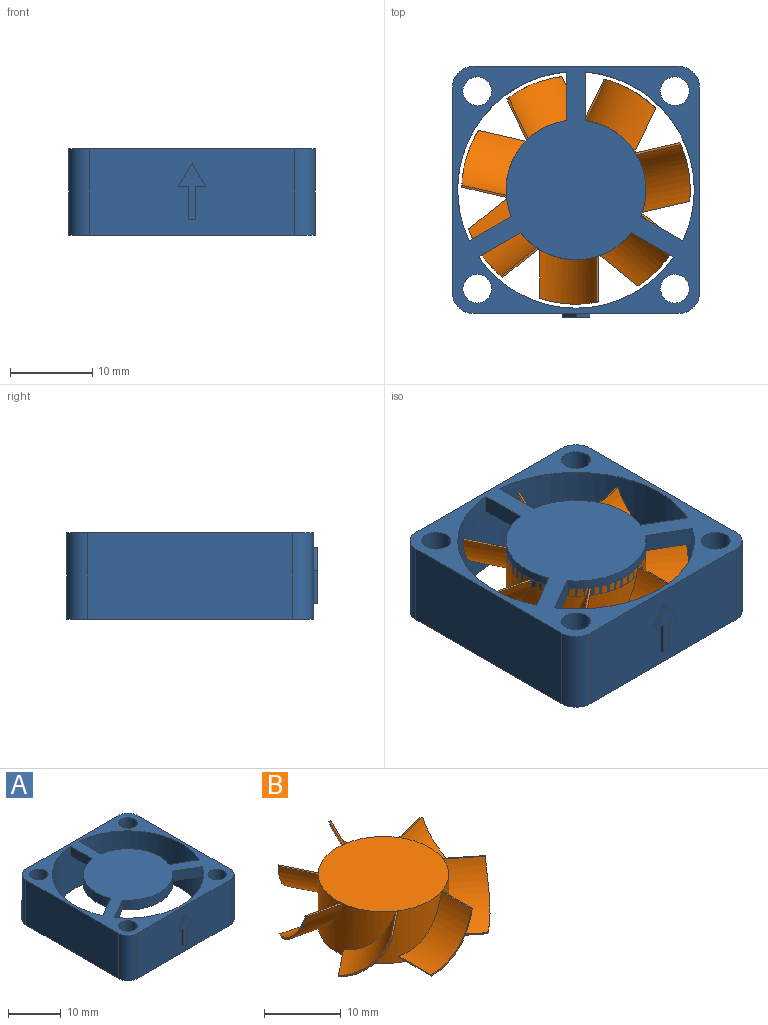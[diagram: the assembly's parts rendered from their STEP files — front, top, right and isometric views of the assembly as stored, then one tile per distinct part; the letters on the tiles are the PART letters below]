
ASSEMBLY  parts=2 mates=1
PART A: 33 faces, bbox 30x30.5x10.5 mm
  f0: cylinder r=2.5mm len=10.5mm, axis (0,0,-1), area 41.2mm2, adj f16,f25,f26,f28
  f1: cylinder r=2.5mm len=10.5mm, axis (0,0,1), area 41.2mm2, adj f4,f16,f25,f26
  f2: cylinder r=2.5mm len=10.5mm, axis (0,0,1), area 41.2mm2, adj f16,f26,f28,f29
  f3: cylinder r=14.38mm len=28.75mm, axis (0,0,1), area 932.8mm2, adj f7,f10,f11,f12,f13,f14,f15,f16
  f4: plane 25x10.5mm, normal (1,0,0), area 262.5mm2, adj f1,f5,f16,f26
  f5: cylinder r=2.5mm len=10.5mm, axis (0,0,-1), area 41.2mm2, adj f4,f16,f26,f29
  f6: cylinder r=8.5mm len=11.64mm, axis (0,0,-1), area 34.9mm2, adj f7,f14,f15,f26
  f7: plane 5.12x2.95mm, normal (0.5,0.87,0), area 13.3mm2, adj f3,f6,f15,f26
  f8: cylinder r=8.5mm len=11.64mm, axis (0,0,-1), area 34.9mm2, adj f12,f13,f15,f26
  f9: cylinder r=8.5mm len=13.44mm, axis (0,0,-1), area 34.9mm2, adj f10,f11,f15,f26
  f10: plane 5.12x2.95mm, normal (-0.5,-0.87,0), area 13.3mm2, adj f3,f9,f15,f26
  f11: plane 5.12x2.95mm, normal (0.5,-0.87,0), area 13.3mm2, adj f3,f9,f15,f26
  f12: plane 5.12x2.95mm, normal (-0.5,0.87,0), area 13.3mm2, adj f3,f8,f15,f26
  f13: plane 5.91x2.25mm, normal (-1,0,0), area 13.3mm2, adj f3,f8,f15,f26
  f14: plane 5.91x2.25mm, normal (1,0,0), area 13.3mm2, adj f3,f6,f15,f26
  f15: plane 25.97x22.88mm, normal (0,0,-1), area 267.6mm2, adj f3,f6,f7,f8,f9,f10,f11,f12
  f16: plane 30x30mm, normal (0,0,-1), area 207mm2, adj f0,f1,f2,f3,f4,f5,f25,f27
  f17: plane 0.95x0.5mm, normal (0,0,-1), area 0.5mm2, adj f18,f19,f24,f25
  f18: plane 4.03x0.5mm, normal (1,0,0), area 2mm2, adj f17,f20,f24,f25
  f19: plane 4.03x0.5mm, normal (-1,0,0), area 2mm2, adj f17,f23,f24,f25
  f20: plane 1.22x0.5mm, normal (0,0,-1), area 0.6mm2, adj f18,f21,f24,f25
  f21: plane 2.81x1.7mm, normal (0.86,0,0.52), area 1.6mm2, adj f20,f22,f24,f25
  f22: plane 2.81x1.7mm, normal (-0.86,0,0.52), area 1.6mm2, adj f21,f23,f24,f25
  f23: plane 1.22x0.5mm, normal (0,0,-1), area 0.6mm2, adj f19,f22,f24,f25
  f24: plane 6.84x3.39mm, normal (0,-1,0), area 8.6mm2, adj f17,f18,f19,f20,f21,f22,f23
  f25: plane 25x10.5mm, normal (0,-1,0), area 253.9mm2, adj f0,f1,f16,f17,f18,f19,f20,f21
  f26: plane 30x30mm, normal (0,0,1), area 474.6mm2, adj f0,f1,f2,f3,f4,f5,f6,f7
  f27: cylinder r=1.75mm len=10.5mm, axis (0,0,1), area 115.5mm2, adj f16,f26
  f28: plane 25x10.5mm, normal (-1,0,0), area 262.5mm2, adj f0,f2,f16,f26
  f29: plane 25x10.5mm, normal (0,1,0), area 262.5mm2, adj f2,f5,f16,f26
  f30: cylinder r=1.75mm len=10.5mm, axis (0,0,1), area 115.5mm2, adj f16,f26
  f31: cylinder r=1.75mm len=10.5mm, axis (0,0,1), area 115.5mm2, adj f16,f26
  f32: cylinder r=1.75mm len=10.5mm, axis (0,0,1), area 115.5mm2, adj f16,f26
PART B: 39 faces, bbox 28.2x28.1x8.3 mm
  f0: cylinder r=10.55mm len=9.5mm, axis (0.78,0.62,0), area 61.5mm2, adj f1,f19,f25,f37
  f1: cylinder r=13.88mm len=7.49mm, axis (0,0,1), area 2.7mm2, adj f0,f19,f20,f25
  f2: cylinder r=10.3mm len=7.25mm, axis (0,1,0), area 60mm2, adj f10,f11,f26,f37
  f3: cylinder r=10.3mm len=9.42mm, axis (-0.78,0.62,0), area 60mm2, adj f7,f22,f27,f37
  f4: plane 5.75x1.39mm, normal (0.21,-0.93,-0.29), area 1.5mm2, adj f5,f8,f28,f37
  f5: cylinder r=10.3mm len=8.21mm, axis (-0.97,-0.22,0), area 55.8mm2, adj f4,f28,f33,f37,f38
  f6: cylinder r=10.55mm len=9.5mm, axis (-0.78,0.62,0), area 61.5mm2, adj f7,f22,f27,f37
  f7: plane 4.44x3.69mm, normal (0.16,0.2,0.97), area 1.4mm2, adj f3,f6,f27,f37
  f8: cylinder r=10.55mm len=8.35mm, axis (-0.97,-0.22,0), area 57.2mm2, adj f4,f28,f33,f37
  f9: cylinder r=10.55mm len=7.43mm, axis (0,1,0), area 61.5mm2, adj f10,f11,f26,f37
  f10: plane 5.92x0.24mm, normal (-0.96,0,-0.29), area 1.5mm2, adj f2,f9,f26,f37
  f11: plane 5.61x0.24mm, normal (0.25,0,0.97), area 1.4mm2, adj f2,f9,f26,f37
  f12: cylinder r=10.3mm len=9.04mm, axis (0.43,-0.9,0), area 60mm2, adj f16,f18,f30,f37
  f13: plane 5.78x1.38mm, normal (0.21,0.93,-0.29), area 1.5mm2, adj f14,f17,f31,f37
  f14: cylinder r=10.3mm len=8.21mm, axis (0.97,-0.22,0), area 60mm2, adj f13,f24,f31,f37
  f15: cylinder r=10.55mm len=9.15mm, axis (0.43,-0.9,0), area 61.5mm2, adj f16,f18,f30,f37
  f16: plane 5.16x2.59mm, normal (-0.23,-0.11,0.97), area 1.4mm2, adj f12,f15,f30,f37
  f17: cylinder r=10.55mm len=8.36mm, axis (0.97,-0.22,0), area 61.5mm2, adj f13,f24,f31,f37
  f18: plane 5.31x2.63mm, normal (0.86,0.41,-0.29), area 1.5mm2, adj f12,f15,f30,f37
  f19: plane 4.62x3.74mm, normal (-0.6,0.75,-0.29), area 1.5mm2, adj f0,f1,f20,f37
  f20: cylinder r=10.3mm len=9.42mm, axis (0.78,0.62,0), area 60mm2, adj f1,f19,f25,f37
  f21: plane 17x17mm, normal (0,0,-1), area 227mm2, adj f37
  f22: plane 4.67x3.71mm, normal (-0.6,-0.75,-0.29), area 1.5mm2, adj f3,f6,f27,f37
  f23: plane 5.36x2.61mm, normal (0.86,-0.42,-0.29), area 1.5mm2, adj f29,f34,f35,f37
  f24: plane 5.42x1.49mm, normal (-0.06,-0.25,0.97), area 1.4mm2, adj f14,f17,f31,f37
  f25: plane 4.54x3.6mm, normal (0.16,-0.2,0.97), area 1.4mm2, adj f0,f1,f20,f37
  f26: cylinder r=13.88mm len=7.49mm, axis (0,0,1), area 2.7mm2, adj f2,f9,f10,f11
  f27: cylinder r=13.88mm len=7.49mm, axis (0,0,1), area 2.7mm2, adj f3,f6,f7,f22
  f28: cylinder r=13.88mm len=7.49mm, axis (0,0,1), area 2.7mm2, adj f4,f5,f8,f33
  f29: cylinder r=13.88mm len=7.49mm, axis (0,0,1), area 2.7mm2, adj f23,f32,f34,f35
  f30: cylinder r=13.88mm len=7.49mm, axis (0,0,1), area 2.7mm2, adj f12,f15,f16,f18
  f31: cylinder r=13.88mm len=7.49mm, axis (0,0,1), area 2.7mm2, adj f13,f14,f17,f24
  f32: plane 5.04x2.65mm, normal (-0.23,0.11,0.97), area 1.4mm2, adj f29,f34,f35,f37
  f33: plane 5.52x1.45mm, normal (-0.06,0.25,0.97), area 1.4mm2, adj f5,f8,f28,f37
  f34: cylinder r=10.55mm len=9.16mm, axis (-0.43,-0.9,0), area 61.5mm2, adj f23,f29,f32,f37
  f35: cylinder r=10.3mm len=9.04mm, axis (-0.43,-0.9,0), area 60mm2, adj f23,f29,f32,f37
  f36: plane 17x17mm, normal (0,0,1), area 227mm2, adj f37,f38
  f37: cylinder r=8.5mm len=17mm, axis (0,0,-1), area 404.2mm2, adj f0,f2,f3,f4,f5,f6,f7,f8
  f38: cylinder r=8.5mm len=6.08mm, axis (0,0,-1), area 13.6mm2, adj f5,f36,f37
PLACE A at identity fixed
PLACE B t=(0,0,1.13)mm
MATE fastened B.f1 <-> A.f3  axis (0,0,-1) through (0,0,5.25)mm
